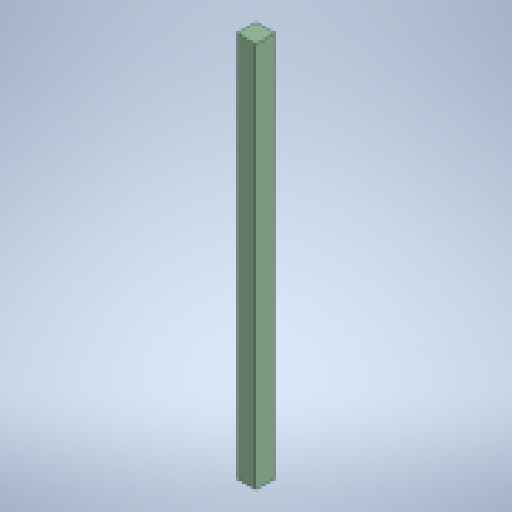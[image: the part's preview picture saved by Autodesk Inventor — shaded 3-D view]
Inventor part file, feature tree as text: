
AUTODESK INVENTOR PART (.ipt)
format: ipt  version: 2025.1 (Build 291241020, 241B)  size: 137,728 bytes
history: native  units: in
note: dims shown in document units (in); Inventor stores cm internally (conversion verified against a paired STEP export)
features: extrude x1, sketch x1, other x1
ambient origin geometry x8: Origin, YZ Plane, XZ Plane, XY Plane, X Axis, Y Axis, Z Axis, Center Point
bodies: Solid1 (feature_tree)
feature tree (3):
  extrude  "Extrusion1"  Depth=3.5in
  sketch  "Sketch1"  dims[d0=3.5in d1=3.5in d2=72.0in d3=0.0in]
  other  "Finish1"
